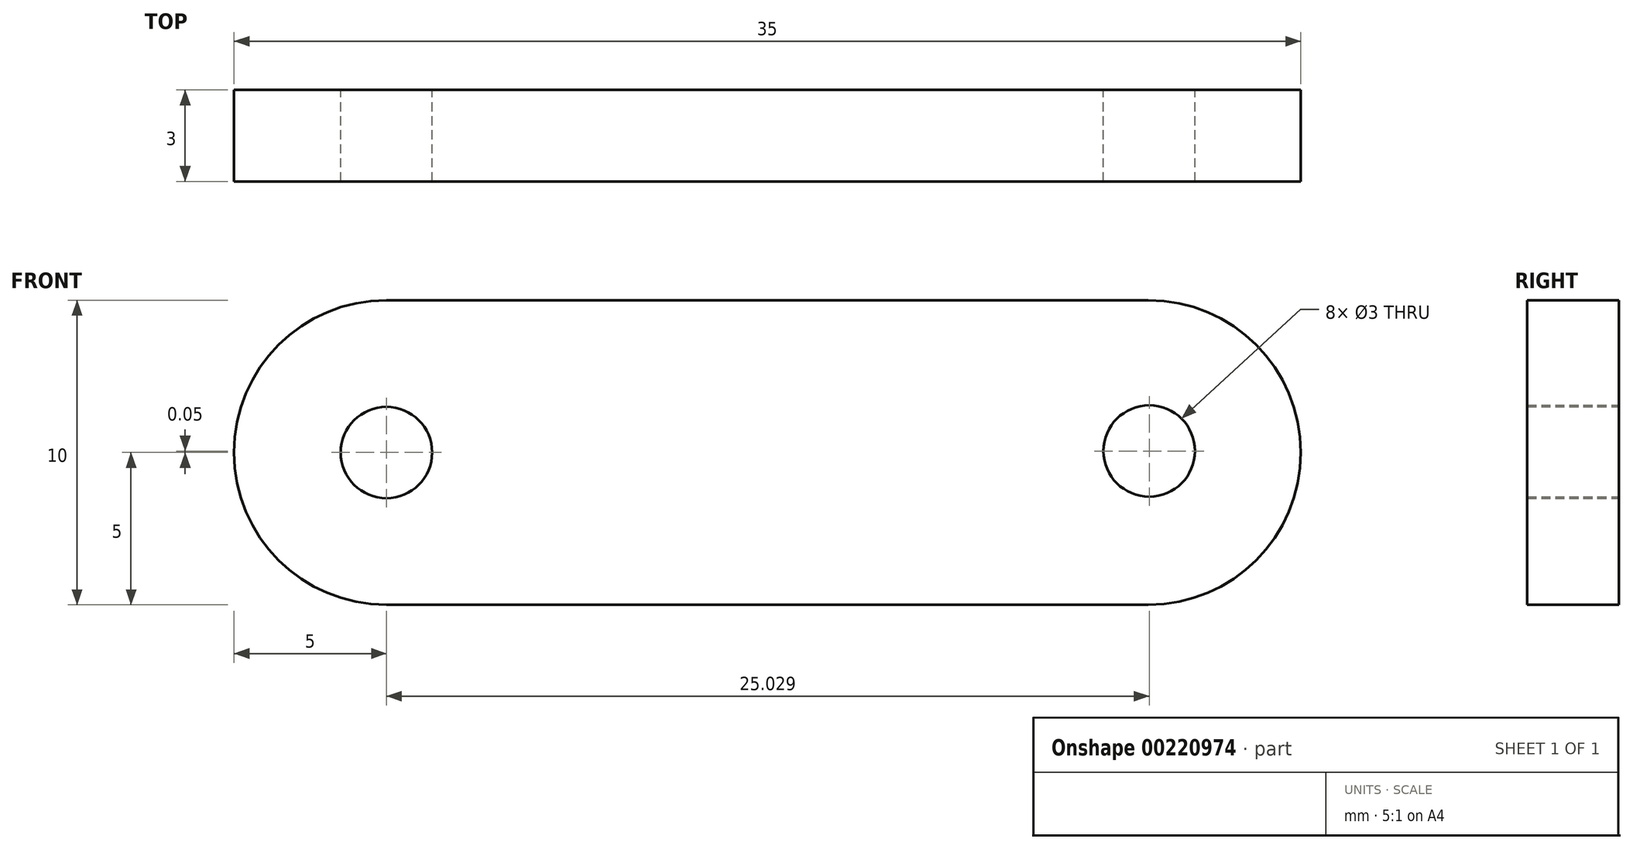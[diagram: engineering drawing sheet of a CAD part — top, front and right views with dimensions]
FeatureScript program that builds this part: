
annotation { "Feature Type Name" : "Feature", "Feature Type Description" : "" }
export const myFeature = defineFeature(function(context is Context, id is Id, definition is map)
    precondition{}
    {
        {
            var Q0;
            Q0=qCreatedBy(makeId("Front.planeOp"),FACE);
            var sketch = newSketch(context, id + "F0", { "sketchPlane" : qUnion([Q0])});
            skPoint(sketch, "E0.endSnap0", {"position": v(12.5, 0) * mm});
            skCircle(sketch, "E1", {"center": v(-25, 0) * mm, "radius": 1.5 * mm});
            skArc(sketch, "E2", {"start": v(-25, 5) * mm, "mid": v(-30, 0) * mm, "end": v(-25, -5) * mm});
            skCircle(sketch, "E3", {"center": v(0.03, 0.05) * mm, "radius": 1.5 * mm});
            skLineSegment(sketch, "E4", {"start": v(-25, -5) * mm, "end": v(0, -5) * mm});
            skLineSegment(sketch, "E5", {"start": v(-25, 5) * mm, "end": v(0, 5) * mm});
            skArc(sketch, "E6", {"start": v(0, -5) * mm, "mid": v(5, 0) * mm, "end": v(0, 5) * mm});
            skSolve(sketch);
        }
        {
            var Q0;
            Q0=makeQuery(id+"F0.imprint","IMPRINT",FACE,{"disambiguationData":[TD([[makeQuery(id+"F0.imprint","IMPRINT",EDGE,{"derivedFrom":sQuery(id+"F0.wireOp",EDGE,"E1")}),-1.0]])]});
            extrude(context, id + "F1", {"entities" : qUnion([Q0]), "depth" : 3 * mm});
        }
    });
